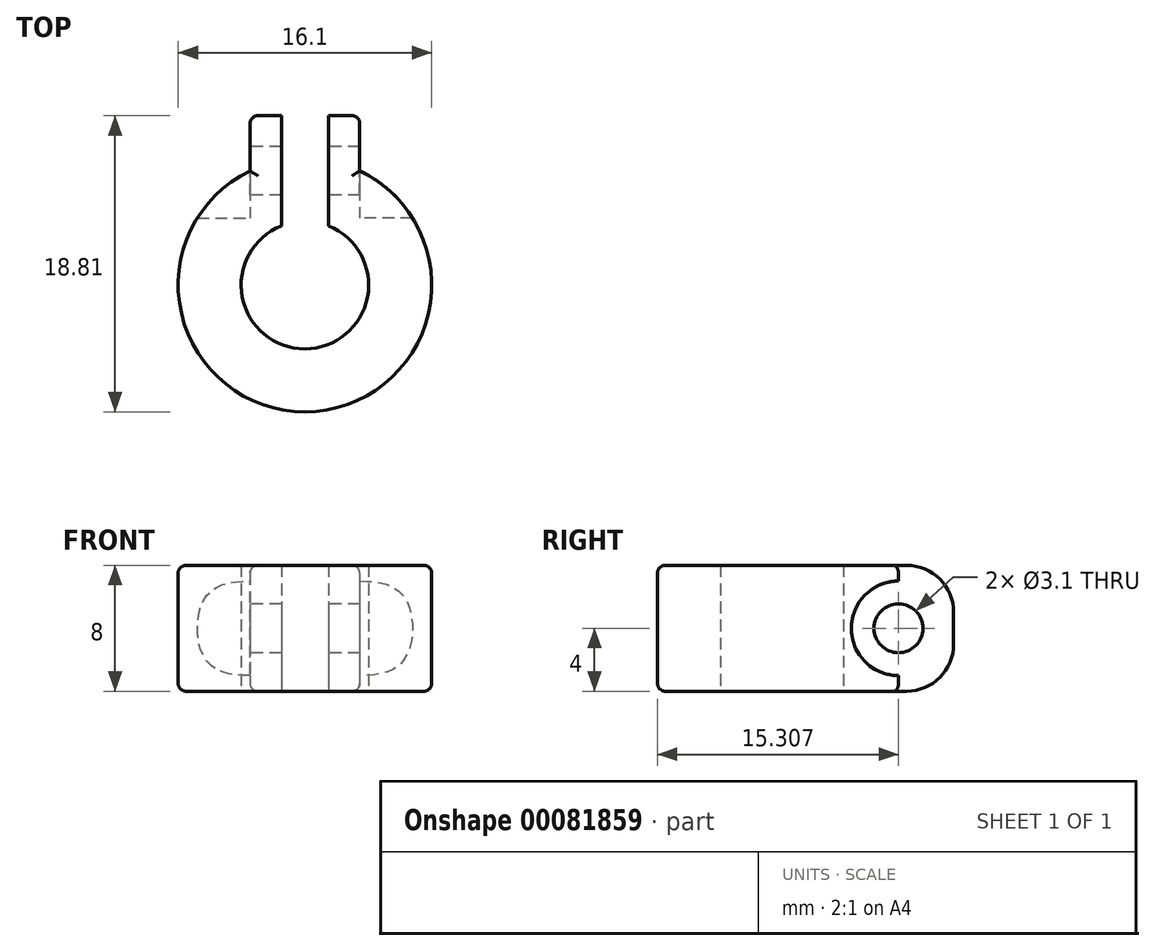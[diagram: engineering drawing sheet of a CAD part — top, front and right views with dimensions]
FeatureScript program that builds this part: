
annotation { "Feature Type Name" : "Feature", "Feature Type Description" : "" }
export const myFeature = defineFeature(function(context is Context, id is Id, definition is map)
    precondition{}
    {
        {
            var Q0;
            Q0=qCreatedBy(makeId("Top.planeOp"),FACE);
            var sketch = newSketch(context, id + "F0", { "sketchPlane" : qUnion([Q0])});
            skArc(sketch, "E0", {"start": v(-1.5, 3.76) * mm, "mid": v(0, -4.05) * mm, "end": v(1.5, 3.76) * mm});
            skArc(sketch, "E1.0", {"start": v(-3.48, 7.26) * mm, "mid": v(0, -8.05) * mm, "end": v(3.48, 7.26) * mm});
            skLineSegment(sketch, "E2.left", {"start": v(1.5, 7.9) * mm, "end": v(1.5, 3.76) * mm});
            skLineSegment(sketch, "E2.right", {"start": v(-1.5, 7.9) * mm, "end": v(-1.5, 3.76) * mm});
            skLineSegment(sketch, "E3.top", {"start": v(-1.5, 9.76) * mm, "end": v(-3.48, 9.76) * mm});
            skLineSegment(sketch, "E3.left", {"start": v(-1.5, 3.76) * mm, "end": v(-1.5, 9.76) * mm});
            skLineSegment(sketch, "E3.right", {"start": v(-3.48, 7.26) * mm, "end": v(-3.48, 9.76) * mm});
            skLineSegment(sketch, "E4.MirrorCS", {"start": v(1.5, 9.76) * mm, "end": v(3.48, 9.76) * mm});
            skLineSegment(sketch, "E5.MirrorCS", {"start": v(3.48, 7.26) * mm, "end": v(3.48, 9.76) * mm});
            skLineSegment(sketch, "E6.MirrorCS", {"start": v(1.5, 3.76) * mm, "end": v(1.5, 9.76) * mm});
            skSolve(sketch);
        }
        {
            var Q0;
            Q0 = qSketchRegion(id + "F0", true);
            extrude(context, id + "F1", {"entities" : qUnion([Q0]), "depth" : 8 * mm});
        }
        {
            var Q0;
            Q0=qCreatedBy(makeId("Right.planeOp"),FACE);
            var sketch = newSketch(context, id + "F2", { "sketchPlane" : qUnion([Q0])});
            skCircle(sketch, "E7", {"center": v(7.26, 4) * mm, "radius": 1.55 * mm});
            skSolve(sketch);
        }
        {
            var Q0;
            Q0 = qSketchRegion(id + "F2", true);
            extrude(context, id + "F3", {"entities" : qUnion([Q0]), "operationType" : NewBodyOperationType.REMOVE, "endBound" : BoundingType.SYMMETRIC, "depth" : 25 * mm});
        }
        {
            var Q0;
            Q0=makeQuery(id+"F1.opExtrude","SWEPT_FACE",FACE,{"disambiguationData":[OSD([sQuery(id+"F0.wireOp",EDGE,"E4.MirrorCS")])]});
            var Q1;
            Q1=makeQuery(id+"F1.opExtrude","SWEPT_FACE",FACE,{"disambiguationData":[OSD([sQuery(id+"F0.wireOp",EDGE,"E3.top")])]});
            extrude(context, id + "F4", {"entities" : qUnion([Q0, Q1]), "operationType" : NewBodyOperationType.ADD, "depth" : 1 * mm});
        }
        {
            var Q0;
            {var subQ0=sQuery(id+"F0.wireOp",EDGE,"E5.MirrorCS");Q0=makeQuery(id+"F4.boolean.opBoolean","MERGE",FACE,{"derivedFrom":[makeQuery(id+"F1.opExtrude","SWEPT_FACE",FACE,{"disambiguationData":[OSD([subQ0])]}),makeQuery(id+"F4.opExtrude","SWEPT_FACE",FACE,{"disambiguationData":[OSD([sQuery(id+"F0.wireOp",EDGE,"E4.MirrorCS"),subQ0])]})]});}
            var sketch = newSketch(context, id + "F5", { "sketchPlane" : qUnion([Q0])});
            skPoint(sketch, "E8.0", {"position": v(7.26, 4) * mm});
            skCircle(sketch, "E9", {"center": v(7.26, 4) * mm, "radius": 3 * mm});
            skSolve(sketch);
        }
        {
            var Q0;
            {var subQ2=sQuery(id+"F0.wireOp",EDGE,"E5.MirrorCS");var subQ9=makeQuery(id+"F3.opExtrude","SWEPT_FACE",FACE,{"disambiguationData":[OSD([sQuery(id+"F2.wireOp",EDGE,"E7")])]});var subQ11=makeQuery(id+"F1.opExtrude","SWEPT_FACE",FACE,{"disambiguationData":[OSD([subQ2])]});var subQ17=makeQuery(id+"F3.boolean.opBoolean","INTERSECT",EDGE,{"derivedFrom":[subQ11,subQ9]});Q0=makeQuery(id+"F5.imprint","IMPRINT",FACE,{"disambiguationData":[TD([[makeQuery(id+"F5.imprint","IMPRINT",EDGE,{"derivedFrom":subQ17}),1.0]])]});}
            extrude(context, id + "F6", {"entities" : qUnion([Q0]), "operationType" : NewBodyOperationType.REMOVE, "depth" : 25 * mm});
        }
        {
            var Q0;
            {var subQ0=sQuery(id+"F0.wireOp",EDGE,"E3.right");Q0=makeQuery(id+"F4.boolean.opBoolean","MERGE",FACE,{"derivedFrom":[makeQuery(id+"F1.opExtrude","SWEPT_FACE",FACE,{"disambiguationData":[OSD([subQ0])]}),makeQuery(id+"F4.opExtrude","SWEPT_FACE",FACE,{"disambiguationData":[OSD([sQuery(id+"F0.wireOp",EDGE,"E3.top"),subQ0])]})]});}
            var sketch = newSketch(context, id + "F7", { "sketchPlane" : qUnion([Q0])});
            skPoint(sketch, "E10.0", {"position": v(-7.26, 4) * mm});
            skCircle(sketch, "E11", {"center": v(-7.26, 4) * mm, "radius": 3 * mm});
            skSolve(sketch);
        }
        {
            var Q0;
            {var subQ4=sQuery(id+"F0.wireOp",EDGE,"E3.right");var subQ9=makeQuery(id+"F3.opExtrude","SWEPT_FACE",FACE,{"disambiguationData":[OSD([sQuery(id+"F2.wireOp",EDGE,"E7")])]});var subQ11=makeQuery(id+"F1.opExtrude","SWEPT_FACE",FACE,{"disambiguationData":[OSD([subQ4])]});var subQ17=makeQuery(id+"F3.boolean.opBoolean","INTERSECT",EDGE,{"derivedFrom":[subQ11,subQ9]});Q0=makeQuery(id+"F7.imprint","IMPRINT",FACE,{"disambiguationData":[TD([[makeQuery(id+"F7.imprint","IMPRINT",EDGE,{"derivedFrom":subQ17}),-1.0]])]});}
            extrude(context, id + "F8", {"entities" : qUnion([Q0]), "operationType" : NewBodyOperationType.REMOVE, "depth" : 25 * mm});
        }
        {
            var Q0;
            {var subQ0=sQuery(id+"F0.wireOp",EDGE,"E4.MirrorCS");Q0=makeQuery(id+"F4.opExtrude","CAP_EDGE",EDGE,{"disambiguationData":[OSD([subQ0]),TDD([makeQuery(id+"F1.opExtrude","CAP_EDGE",EDGE,{"disambiguationData":[OSD([subQ0])],"isStart":false})])],"isStart":false});}
            var Q1;
            {var subQ0=sQuery(id+"F0.wireOp",EDGE,"E4.MirrorCS");Q1=makeQuery(id+"F4.opExtrude","CAP_EDGE",EDGE,{"disambiguationData":[OSD([subQ0]),TDD([makeQuery(id+"F1.opExtrude","CAP_EDGE",EDGE,{"disambiguationData":[OSD([subQ0])],"isStart":true})])],"isStart":false});}
            fillet(context, id + "F9", {"entities" : qUnion([Q0, Q1]), "radius" : 3 * mm, "tangentPropagation" : true, "allowEdgeOverflow" : false});
        }
        {
            var Q0;
            {var subQ0=sQuery(id+"F0.wireOp",EDGE,"E3.top");Q0=makeQuery(id+"F4.opExtrude","CAP_EDGE",EDGE,{"disambiguationData":[OSD([subQ0]),TDD([makeQuery(id+"F1.opExtrude","CAP_EDGE",EDGE,{"disambiguationData":[OSD([subQ0])],"isStart":false})])],"isStart":false});}
            var Q1;
            {var subQ0=sQuery(id+"F0.wireOp",EDGE,"E3.top");Q1=makeQuery(id+"F4.opExtrude","CAP_EDGE",EDGE,{"disambiguationData":[OSD([subQ0]),TDD([makeQuery(id+"F1.opExtrude","CAP_EDGE",EDGE,{"disambiguationData":[OSD([subQ0])],"isStart":true})])],"isStart":false});}
            fillet(context, id + "F10", {"entities" : qUnion([Q0, Q1]), "radius" : 3 * mm, "tangentPropagation" : true, "allowEdgeOverflow" : false});
        }
        {
            var Q0;
            {var subQ0=sQuery(id+"F0.wireOp",EDGE,"E3.right");var subQ1=sQuery(id+"F0.wireOp",EDGE,"E3.top");Q0=makeQuery(id+"F10.opFillet","BLEND_EDGE",EDGE,{"blendedFrom":[makeQuery(id+"F4.opExtrude","CAP_EDGE",EDGE,{"disambiguationData":[OSD([subQ1]),TDD([makeQuery(id+"F1.opExtrude","CAP_EDGE",EDGE,{"disambiguationData":[OSD([subQ1])],"isStart":false})])],"isStart":false}),makeQuery(id+"F8.boolean.opBoolean","MERGE",FACE,{"derivedFrom":[makeQuery(id+"F4.boolean.opBoolean","MERGE",FACE,{"derivedFrom":[makeQuery(id+"F1.opExtrude","SWEPT_FACE",FACE,{"disambiguationData":[OSD([subQ0])]}),makeQuery(id+"F4.opExtrude","SWEPT_FACE",FACE,{"disambiguationData":[OSD([subQ1,subQ0])]})]}),makeQuery(id+"F8.opExtrude","CAP_FACE",FACE,{"disambiguationData":[OSD([sQuery(id+"F0.wireOp",EDGE,"E1.0"),subQ0,sQuery(id+"F2.wireOp",EDGE,"E7"),sQuery(id+"F7.wireOp",EDGE,"E11")])],"isStart":true})]})],"blendedInto":[makeQuery(id+"F8.boolean.opBoolean","MERGE",FACE,{"derivedFrom":[makeQuery(id+"F4.boolean.opBoolean","MERGE",FACE,{"derivedFrom":[makeQuery(id+"F1.opExtrude","SWEPT_FACE",FACE,{"disambiguationData":[OSD([subQ0])]}),makeQuery(id+"F4.opExtrude","SWEPT_FACE",FACE,{"disambiguationData":[OSD([subQ1,subQ0])]})]}),makeQuery(id+"F8.opExtrude","CAP_FACE",FACE,{"disambiguationData":[OSD([sQuery(id+"F0.wireOp",EDGE,"E1.0"),subQ0,sQuery(id+"F2.wireOp",EDGE,"E7"),sQuery(id+"F7.wireOp",EDGE,"E11")])],"isStart":true})]})]});}
            var Q1;
            {var subQ0=sQuery(id+"F0.wireOp",EDGE,"E3.right");var subQ1=sQuery(id+"F0.wireOp",EDGE,"E3.top");Q1=makeQuery(id+"F4.boolean.opBoolean","MERGE",EDGE,{"derivedFrom":[makeQuery(id+"F1.opExtrude","CAP_EDGE",EDGE,{"disambiguationData":[OSD([subQ0])],"isStart":false}),makeQuery(id+"F4.opExtrude","SWEPT_EDGE",EDGE,{"disambiguationData":[OSD([subQ1,subQ0]),TDD([makeQuery(id+"F1.opExtrude","CAP_VERTEX",VERTEX,{"disambiguationData":[OSD([subQ1,subQ0])],"isStart":false})])]})]});}
            var Q2;
            Q2=makeQuery(id+"F1.opExtrude","CAP_EDGE",EDGE,{"disambiguationData":[OSD([sQuery(id+"F0.wireOp",EDGE,"E1.0")])],"isStart":false});
            var Q3;
            {var subQ0=sQuery(id+"F0.wireOp",EDGE,"E5.MirrorCS");var subQ1=sQuery(id+"F0.wireOp",EDGE,"E4.MirrorCS");Q3=makeQuery(id+"F4.boolean.opBoolean","MERGE",EDGE,{"derivedFrom":[makeQuery(id+"F1.opExtrude","CAP_EDGE",EDGE,{"disambiguationData":[OSD([subQ0])],"isStart":false}),makeQuery(id+"F4.opExtrude","SWEPT_EDGE",EDGE,{"disambiguationData":[OSD([subQ1,subQ0]),TDD([makeQuery(id+"F1.opExtrude","CAP_VERTEX",VERTEX,{"disambiguationData":[OSD([subQ1,subQ0])],"isStart":false})])]})]});}
            var Q4;
            {var subQ0=sQuery(id+"F0.wireOp",EDGE,"E5.MirrorCS");var subQ1=sQuery(id+"F0.wireOp",EDGE,"E4.MirrorCS");Q4=makeQuery(id+"F9.opFillet","BLEND_EDGE",EDGE,{"blendedFrom":[makeQuery(id+"F4.opExtrude","CAP_EDGE",EDGE,{"disambiguationData":[OSD([subQ1]),TDD([makeQuery(id+"F1.opExtrude","CAP_EDGE",EDGE,{"disambiguationData":[OSD([subQ1])],"isStart":false})])],"isStart":false}),makeQuery(id+"F6.boolean.opBoolean","MERGE",FACE,{"derivedFrom":[makeQuery(id+"F4.boolean.opBoolean","MERGE",FACE,{"derivedFrom":[makeQuery(id+"F1.opExtrude","SWEPT_FACE",FACE,{"disambiguationData":[OSD([subQ0])]}),makeQuery(id+"F4.opExtrude","SWEPT_FACE",FACE,{"disambiguationData":[OSD([subQ1,subQ0])]})]}),makeQuery(id+"F6.opExtrude","CAP_FACE",FACE,{"disambiguationData":[OSD([sQuery(id+"F0.wireOp",EDGE,"E1.0"),subQ0,sQuery(id+"F2.wireOp",EDGE,"E7"),sQuery(id+"F5.wireOp",EDGE,"E9")])],"isStart":true})]})],"blendedInto":[makeQuery(id+"F6.boolean.opBoolean","MERGE",FACE,{"derivedFrom":[makeQuery(id+"F4.boolean.opBoolean","MERGE",FACE,{"derivedFrom":[makeQuery(id+"F1.opExtrude","SWEPT_FACE",FACE,{"disambiguationData":[OSD([subQ0])]}),makeQuery(id+"F4.opExtrude","SWEPT_FACE",FACE,{"disambiguationData":[OSD([subQ1,subQ0])]})]}),makeQuery(id+"F6.opExtrude","CAP_FACE",FACE,{"disambiguationData":[OSD([sQuery(id+"F0.wireOp",EDGE,"E1.0"),subQ0,sQuery(id+"F2.wireOp",EDGE,"E7"),sQuery(id+"F5.wireOp",EDGE,"E9")])],"isStart":true})]})]});}
            var Q5;
            Q5=makeQuery(id+"F4.opExtrude","CAP_EDGE",EDGE,{"disambiguationData":[OSD([sQuery(id+"F0.wireOp",EDGE,"E4.MirrorCS"),sQuery(id+"F0.wireOp",EDGE,"E5.MirrorCS")])],"isStart":false});
            var Q6;
            Q6=makeQuery(id+"F4.opExtrude","CAP_EDGE",EDGE,{"disambiguationData":[OSD([sQuery(id+"F0.wireOp",EDGE,"E3.top"),sQuery(id+"F0.wireOp",EDGE,"E3.right")])],"isStart":false});
            var Q7;
            {var subQ0=sQuery(id+"F0.wireOp",EDGE,"E3.right");var subQ1=sQuery(id+"F0.wireOp",EDGE,"E3.top");Q7=makeQuery(id+"F10.opFillet","BLEND_EDGE",EDGE,{"blendedFrom":[makeQuery(id+"F4.opExtrude","CAP_EDGE",EDGE,{"disambiguationData":[OSD([subQ1]),TDD([makeQuery(id+"F1.opExtrude","CAP_EDGE",EDGE,{"disambiguationData":[OSD([subQ1])],"isStart":true})])],"isStart":false}),makeQuery(id+"F8.boolean.opBoolean","MERGE",FACE,{"derivedFrom":[makeQuery(id+"F4.boolean.opBoolean","MERGE",FACE,{"derivedFrom":[makeQuery(id+"F1.opExtrude","SWEPT_FACE",FACE,{"disambiguationData":[OSD([subQ0])]}),makeQuery(id+"F4.opExtrude","SWEPT_FACE",FACE,{"disambiguationData":[OSD([subQ1,subQ0])]})]}),makeQuery(id+"F8.opExtrude","CAP_FACE",FACE,{"disambiguationData":[OSD([sQuery(id+"F0.wireOp",EDGE,"E1.0"),subQ0,sQuery(id+"F2.wireOp",EDGE,"E7"),sQuery(id+"F7.wireOp",EDGE,"E11")])],"isStart":true})]})],"blendedInto":[makeQuery(id+"F8.boolean.opBoolean","MERGE",FACE,{"derivedFrom":[makeQuery(id+"F4.boolean.opBoolean","MERGE",FACE,{"derivedFrom":[makeQuery(id+"F1.opExtrude","SWEPT_FACE",FACE,{"disambiguationData":[OSD([subQ0])]}),makeQuery(id+"F4.opExtrude","SWEPT_FACE",FACE,{"disambiguationData":[OSD([subQ1,subQ0])]})]}),makeQuery(id+"F8.opExtrude","CAP_FACE",FACE,{"disambiguationData":[OSD([sQuery(id+"F0.wireOp",EDGE,"E1.0"),subQ0,sQuery(id+"F2.wireOp",EDGE,"E7"),sQuery(id+"F7.wireOp",EDGE,"E11")])],"isStart":true})]})]});}
            var Q8;
            {var subQ0=sQuery(id+"F0.wireOp",EDGE,"E3.right");var subQ1=sQuery(id+"F0.wireOp",EDGE,"E3.top");Q8=makeQuery(id+"F4.boolean.opBoolean","MERGE",EDGE,{"derivedFrom":[makeQuery(id+"F1.opExtrude","CAP_EDGE",EDGE,{"disambiguationData":[OSD([subQ0])],"isStart":true}),makeQuery(id+"F4.opExtrude","SWEPT_EDGE",EDGE,{"disambiguationData":[OSD([subQ1,subQ0]),TDD([makeQuery(id+"F1.opExtrude","CAP_VERTEX",VERTEX,{"disambiguationData":[OSD([subQ1,subQ0])],"isStart":true})])]})]});}
            var Q9;
            Q9=makeQuery(id+"F1.opExtrude","CAP_EDGE",EDGE,{"disambiguationData":[OSD([sQuery(id+"F0.wireOp",EDGE,"E1.0")])],"isStart":true});
            var Q10;
            {var subQ0=sQuery(id+"F0.wireOp",EDGE,"E5.MirrorCS");var subQ1=sQuery(id+"F0.wireOp",EDGE,"E4.MirrorCS");Q10=makeQuery(id+"F4.boolean.opBoolean","MERGE",EDGE,{"derivedFrom":[makeQuery(id+"F1.opExtrude","CAP_EDGE",EDGE,{"disambiguationData":[OSD([subQ0])],"isStart":true}),makeQuery(id+"F4.opExtrude","SWEPT_EDGE",EDGE,{"disambiguationData":[OSD([subQ1,subQ0]),TDD([makeQuery(id+"F1.opExtrude","CAP_VERTEX",VERTEX,{"disambiguationData":[OSD([subQ1,subQ0])],"isStart":true})])]})]});}
            var Q11;
            {var subQ0=sQuery(id+"F0.wireOp",EDGE,"E5.MirrorCS");var subQ1=sQuery(id+"F0.wireOp",EDGE,"E4.MirrorCS");Q11=makeQuery(id+"F9.opFillet","BLEND_EDGE",EDGE,{"blendedFrom":[makeQuery(id+"F4.opExtrude","CAP_EDGE",EDGE,{"disambiguationData":[OSD([subQ1]),TDD([makeQuery(id+"F1.opExtrude","CAP_EDGE",EDGE,{"disambiguationData":[OSD([subQ1])],"isStart":true})])],"isStart":false}),makeQuery(id+"F6.boolean.opBoolean","MERGE",FACE,{"derivedFrom":[makeQuery(id+"F4.boolean.opBoolean","MERGE",FACE,{"derivedFrom":[makeQuery(id+"F1.opExtrude","SWEPT_FACE",FACE,{"disambiguationData":[OSD([subQ0])]}),makeQuery(id+"F4.opExtrude","SWEPT_FACE",FACE,{"disambiguationData":[OSD([subQ1,subQ0])]})]}),makeQuery(id+"F6.opExtrude","CAP_FACE",FACE,{"disambiguationData":[OSD([sQuery(id+"F0.wireOp",EDGE,"E1.0"),subQ0,sQuery(id+"F2.wireOp",EDGE,"E7"),sQuery(id+"F5.wireOp",EDGE,"E9")])],"isStart":true})]})],"blendedInto":[makeQuery(id+"F6.boolean.opBoolean","MERGE",FACE,{"derivedFrom":[makeQuery(id+"F4.boolean.opBoolean","MERGE",FACE,{"derivedFrom":[makeQuery(id+"F1.opExtrude","SWEPT_FACE",FACE,{"disambiguationData":[OSD([subQ0])]}),makeQuery(id+"F4.opExtrude","SWEPT_FACE",FACE,{"disambiguationData":[OSD([subQ1,subQ0])]})]}),makeQuery(id+"F6.opExtrude","CAP_FACE",FACE,{"disambiguationData":[OSD([sQuery(id+"F0.wireOp",EDGE,"E1.0"),subQ0,sQuery(id+"F2.wireOp",EDGE,"E7"),sQuery(id+"F5.wireOp",EDGE,"E9")])],"isStart":true})]})]});}
            fillet(context, id + "F11", {"entities" : qUnion([Q0, Q1, Q2, Q3, Q4, Q5, Q6, Q7, Q8, Q9, Q10, Q11]), "radius" : 0.5 * mm, "tangentPropagation" : true, "allowEdgeOverflow" : false});
        }
    });
